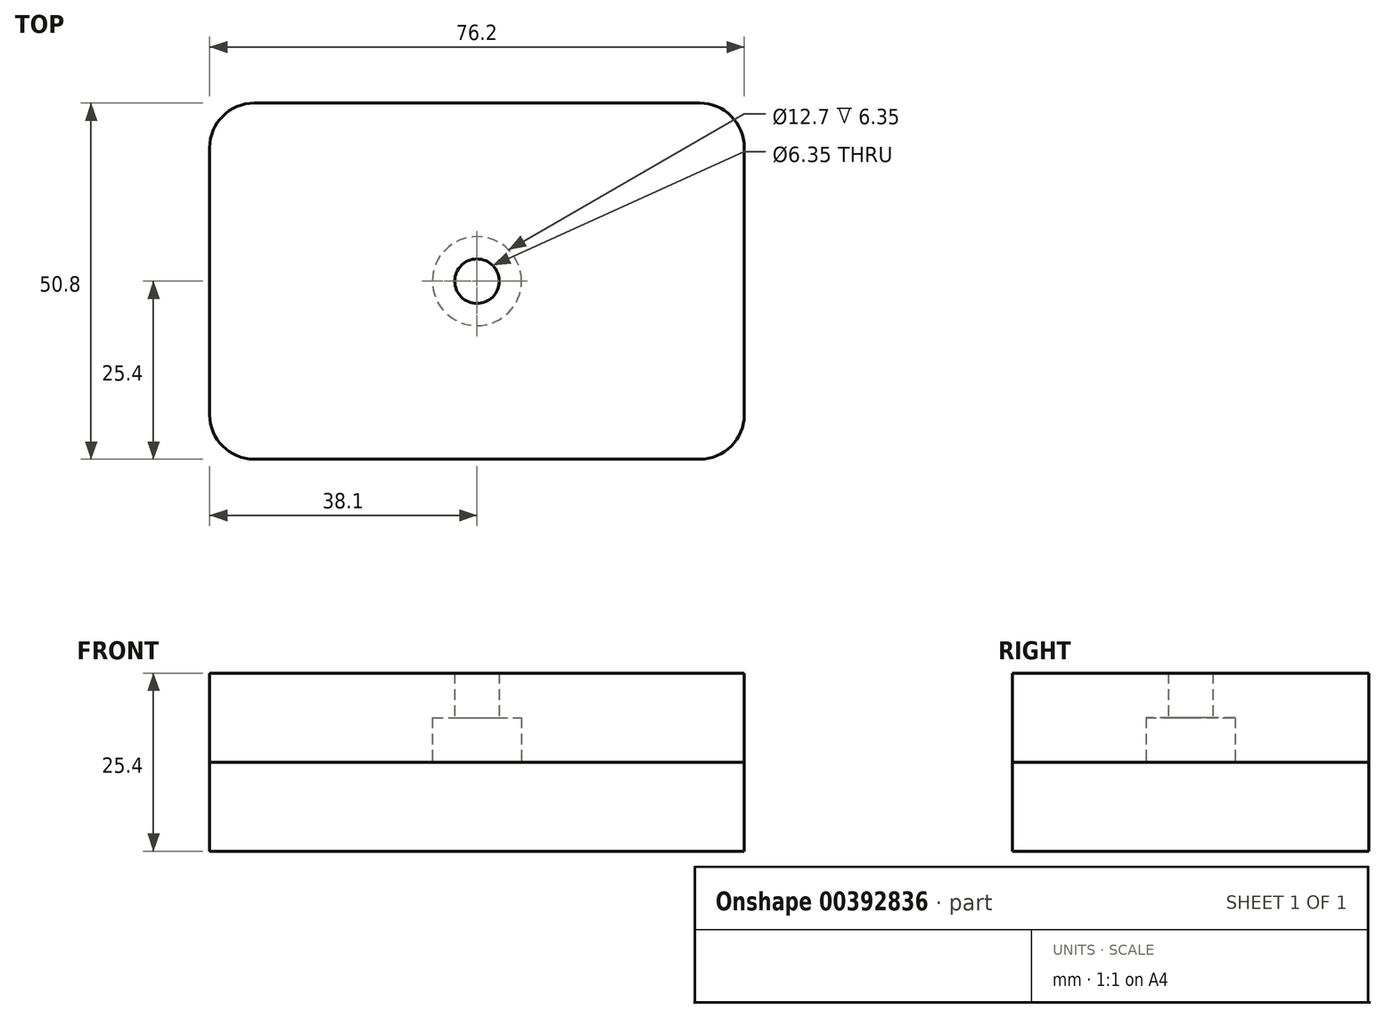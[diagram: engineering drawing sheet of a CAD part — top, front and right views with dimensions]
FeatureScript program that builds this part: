
annotation { "Feature Type Name" : "Feature", "Feature Type Description" : "" }
export const myFeature = defineFeature(function(context is Context, id is Id, definition is map)
    precondition{}
    {
        {
            var Q0;
            Q0=qCreatedBy(makeId("Top.planeOp"),FACE);
            var sketch = newSketch(context, id + "F0", { "sketchPlane" : qUnion([Q0])});
            skLineSegment(sketch, "E0.bottom", {"start": v(-31.75, 25.4) * mm, "end": v(31.75, 25.4) * mm});
            skLineSegment(sketch, "E0.top", {"start": v(-31.75, -25.4) * mm, "end": v(31.75, -25.4) * mm});
            skLineSegment(sketch, "E0.left", {"start": v(-38.1, 19.05) * mm, "end": v(-38.1, -19.05) * mm});
            skLineSegment(sketch, "E0.right", {"start": v(38.1, 19.05) * mm, "end": v(38.1, -19.05) * mm});
            skPoint(sketch, "E0.middle", {"position": v(0, 0) * mm});
            skPoint(sketch, "E1.visualSharp", {"position": v(-38.1, 25.4) * mm});
            skArc(sketch, "E1.filletArc", {"start": v(-31.75, 25.4) * mm, "mid": v(-36.24, 23.54) * mm, "end": v(-38.1, 19.05) * mm});
            skPoint(sketch, "E2.visualSharp", {"position": v(38.1, 25.4) * mm});
            skArc(sketch, "E2.filletArc", {"start": v(38.1, 19.05) * mm, "mid": v(36.24, 23.54) * mm, "end": v(31.75, 25.4) * mm});
            skPoint(sketch, "E3.visualSharp", {"position": v(-38.1, -25.4) * mm});
            skArc(sketch, "E3.filletArc", {"start": v(-38.1, -19.05) * mm, "mid": v(-36.24, -23.54) * mm, "end": v(-31.75, -25.4) * mm});
            skPoint(sketch, "E4.visualSharp", {"position": v(38.1, -25.4) * mm});
            skArc(sketch, "E4.filletArc", {"start": v(31.75, -25.4) * mm, "mid": v(36.24, -23.54) * mm, "end": v(38.1, -19.05) * mm});
            skSolve(sketch);
        }
        {
            var Q0;
            Q0=makeQuery(id+"F0.imprint","IMPRINT",FACE,{"disambiguationData":[TD([[makeQuery(id+"F0.imprint","IMPRINT",EDGE,{"derivedFrom":sQuery(id+"F0.wireOp",EDGE,"E0.bottom")}),-1.0]])]});
            extrude(context, id + "F1", {"entities" : qUnion([Q0]), "depth" : 12.7 * mm});
        }
        {
            var Q0;
            Q0=makeQuery(id+"F1.opExtrude","SWEPT_BODY",BODY,{"disambiguationData":[OSD([sQuery(id+"F0.wireOp",EDGE,"E0.bottom"),sQuery(id+"F0.wireOp",EDGE,"E0.top"),sQuery(id+"F0.wireOp",EDGE,"E0.left"),sQuery(id+"F0.wireOp",EDGE,"E0.right"),sQuery(id+"F0.wireOp",EDGE,"E1.filletArc"),sQuery(id+"F0.wireOp",EDGE,"E2.filletArc"),sQuery(id+"F0.wireOp",EDGE,"E3.filletArc"),sQuery(id+"F0.wireOp",EDGE,"E4.filletArc")])]});
            transform(context, id + "F2", {"entities" : qUnion([Q0]), "transformType" : TransformType.TRANSLATION_3D, "dx" : 0 * mm, "dy" : 0 * mm, "dz" : 12.7 * mm, "makeCopy" : true});
        }
        {
            var Q0;
            Q0=makeQuery(id+"F2.opPattern","COPY",FACE,{"derivedFrom":makeQuery(id+"F1.opExtrude","CAP_FACE",FACE,{"disambiguationData":[OSD([sQuery(id+"F0.wireOp",EDGE,"E0.bottom"),sQuery(id+"F0.wireOp",EDGE,"E0.top"),sQuery(id+"F0.wireOp",EDGE,"E0.left"),sQuery(id+"F0.wireOp",EDGE,"E0.right"),sQuery(id+"F0.wireOp",EDGE,"E1.filletArc"),sQuery(id+"F0.wireOp",EDGE,"E2.filletArc"),sQuery(id+"F0.wireOp",EDGE,"E3.filletArc"),sQuery(id+"F0.wireOp",EDGE,"E4.filletArc")])],"isStart":true}),"instanceName":"1"});
            var sketch = newSketch(context, id + "F3", { "sketchPlane" : qUnion([Q0])});
            skPoint(sketch, "E5.0", {"position": v(0, 0) * mm});
            skCircle(sketch, "E6", {"center": v(0, 0) * mm, "radius": 6.35 * mm});
            skCircle(sketch, "E7", {"center": v(0, 0) * mm, "radius": 3.18 * mm});
            skSolve(sketch);
        }
        {
            var Q0;
            Q0=makeQuery(id+"F3.imprint","IMPRINT",FACE,{"disambiguationData":[TD([[makeQuery(id+"F3.imprint","IMPRINT",EDGE,{"derivedFrom":sQuery(id+"F3.wireOp",EDGE,"E6")}),1.0]])]});
            var Q1;
            Q1=makeQuery(id+"F3.imprint","IMPRINT",FACE,{"disambiguationData":[TD([[makeQuery(id+"F3.imprint","IMPRINT",EDGE,{"derivedFrom":sQuery(id+"F3.wireOp",EDGE,"E7")}),1.0]])]});
            extrude(context, id + "F4", {"entities" : qUnion([Q0, Q1]), "operationType" : NewBodyOperationType.REMOVE, "oppositeDirection" : true, "depth" : 6.35 * mm});
        }
        {
            var Q0;
            Q0=makeQuery(id+"F3.imprint","IMPRINT",FACE,{"disambiguationData":[TD([[makeQuery(id+"F3.imprint","IMPRINT",EDGE,{"derivedFrom":sQuery(id+"F3.wireOp",EDGE,"E7")}),1.0]])]});
            var Q1;
            Q1=makeQuery(id+"F2.opPattern","COPY",FACE,{"derivedFrom":makeQuery(id+"F1.opExtrude","CAP_FACE",FACE,{"disambiguationData":[OSD([sQuery(id+"F0.wireOp",EDGE,"E0.bottom"),sQuery(id+"F0.wireOp",EDGE,"E0.top"),sQuery(id+"F0.wireOp",EDGE,"E0.left"),sQuery(id+"F0.wireOp",EDGE,"E0.right"),sQuery(id+"F0.wireOp",EDGE,"E1.filletArc"),sQuery(id+"F0.wireOp",EDGE,"E2.filletArc"),sQuery(id+"F0.wireOp",EDGE,"E3.filletArc"),sQuery(id+"F0.wireOp",EDGE,"E4.filletArc")])],"isStart":false}),"instanceName":"1"});
            extrude(context, id + "F5", {"entities" : qUnion([Q0]), "operationType" : NewBodyOperationType.REMOVE, "endBound" : BoundingType.UP_TO_SURFACE, "oppositeDirection" : true, "endBoundEntityFace" : qUnion([Q1]), "depth" : 25.4 * mm});
        }
    });
